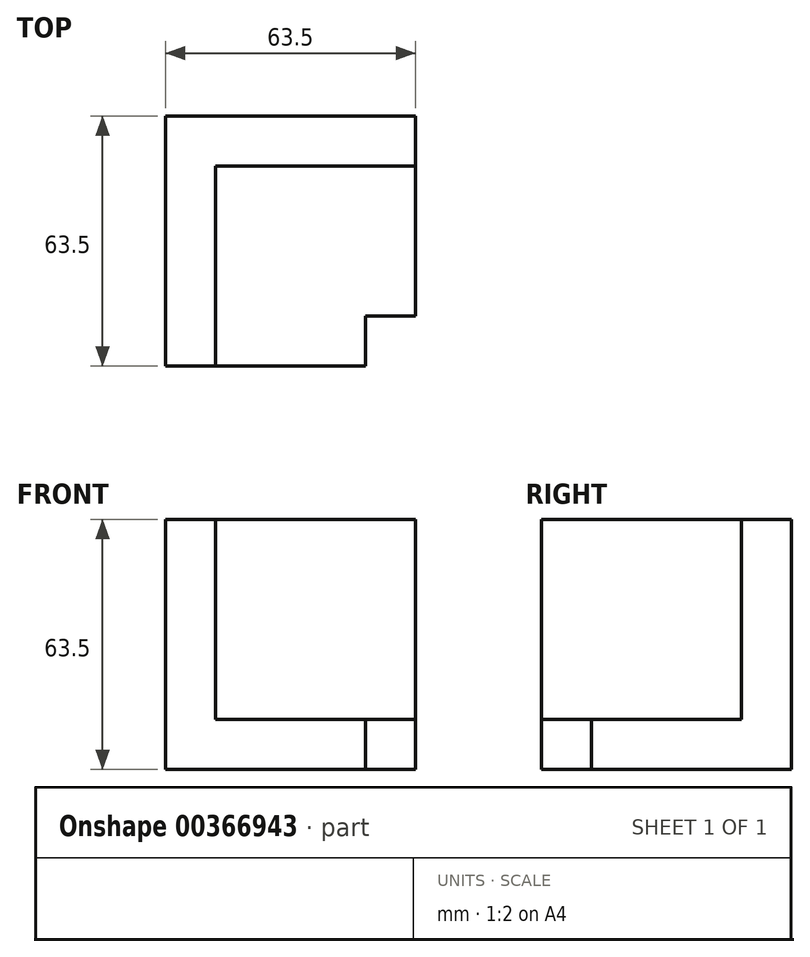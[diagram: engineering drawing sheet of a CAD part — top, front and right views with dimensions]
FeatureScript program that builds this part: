
annotation { "Feature Type Name" : "Feature", "Feature Type Description" : "" }
export const myFeature = defineFeature(function(context is Context, id is Id, definition is map)
    precondition{}
    {
        {
            var Q0;
            Q0=qCreatedBy(makeId("Front.planeOp"),FACE);
            var sketch = newSketch(context, id + "F0", { "sketchPlane" : qUnion([Q0])});
            skLineSegment(sketch, "E0.bottom", {"start": v(0, 0) * mm, "end": v(63.5, 0) * mm});
            skLineSegment(sketch, "E0.top", {"start": v(0, -63.5) * mm, "end": v(63.5, -63.5) * mm});
            skLineSegment(sketch, "E0.left", {"start": v(0, 0) * mm, "end": v(0, -63.5) * mm});
            skLineSegment(sketch, "E0.right", {"start": v(63.5, 0) * mm, "end": v(63.5, -63.5) * mm});
            skSolve(sketch);
        }
        {
            var Q0;
            Q0=makeQuery(id+"F0.imprint","IMPRINT",FACE,{"disambiguationData":[TD([[makeQuery(id+"F0.imprint","IMPRINT",EDGE,{"derivedFrom":sQuery(id+"F0.wireOp",EDGE,"E0.bottom")}),-1.0]])]});
            extrude(context, id + "F1", {"entities" : qUnion([Q0]), "depth" : 63.5 * mm});
        }
        {
            var Q0;
            Q0=makeQuery(id+"F1.opExtrude","SWEPT_FACE",FACE,{"disambiguationData":[OSD([sQuery(id+"F0.wireOp",EDGE,"E0.bottom")])]});
            var sketch = newSketch(context, id + "F2", { "sketchPlane" : qUnion([Q0])});
            skLineSegment(sketch, "E1.bottom", {"start": v(63.5, -63.5) * mm, "end": v(12.7, -63.5) * mm});
            skLineSegment(sketch, "E1.top", {"start": v(63.5, -12.7) * mm, "end": v(12.7, -12.7) * mm});
            skLineSegment(sketch, "E1.left", {"start": v(63.5, -63.5) * mm, "end": v(63.5, -12.7) * mm});
            skLineSegment(sketch, "E1.right", {"start": v(12.7, -63.5) * mm, "end": v(12.7, -12.7) * mm});
            skSolve(sketch);
        }
        {
            var Q0;
            Q0=makeQuery(id+"F2.imprint","IMPRINT",FACE,{"disambiguationData":[TD([[makeQuery(id+"F2.imprint","IMPRINT",EDGE,{"derivedFrom":sQuery(id+"F2.wireOp",EDGE,"E1.bottom")}),1.0]])]});
            extrude(context, id + "F3", {"entities" : qUnion([Q0]), "operationType" : NewBodyOperationType.REMOVE, "oppositeDirection" : true, "depth" : 50.8 * mm});
        }
        {
            var Q0;
            Q0=makeQuery(id+"F3.boolean.opBoolean","COPY",FACE,{"derivedFrom":makeQuery(id+"F3.opExtrude","CAP_FACE",FACE,{"disambiguationData":[OSD([sQuery(id+"F2.wireOp",EDGE,"E1.bottom"),sQuery(id+"F2.wireOp",EDGE,"E1.top"),sQuery(id+"F2.wireOp",EDGE,"E1.left"),sQuery(id+"F2.wireOp",EDGE,"E1.right")])],"isStart":false})});
            var sketch = newSketch(context, id + "F4", { "sketchPlane" : qUnion([Q0])});
            skLineSegment(sketch, "E2.bottom", {"start": v(63.5, -63.5) * mm, "end": v(50.8, -63.5) * mm});
            skLineSegment(sketch, "E2.top", {"start": v(63.5, -50.8) * mm, "end": v(50.8, -50.8) * mm});
            skLineSegment(sketch, "E2.left", {"start": v(63.5, -63.5) * mm, "end": v(63.5, -50.8) * mm});
            skLineSegment(sketch, "E2.right", {"start": v(50.8, -63.5) * mm, "end": v(50.8, -50.8) * mm});
            skSolve(sketch);
        }
        {
            var Q0;
            Q0=makeQuery(id+"F4.imprint","IMPRINT",FACE,{"disambiguationData":[TD([[makeQuery(id+"F4.imprint","IMPRINT",EDGE,{"derivedFrom":sQuery(id+"F4.wireOp",EDGE,"E2.bottom")}),1.0]])]});
            extrude(context, id + "F5", {"entities" : qUnion([Q0]), "operationType" : NewBodyOperationType.REMOVE, "oppositeDirection" : true, "depth" : 12.7 * mm});
        }
    });
